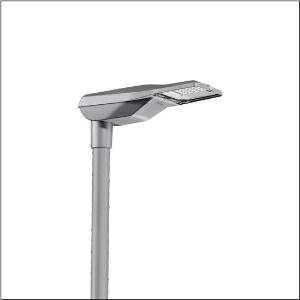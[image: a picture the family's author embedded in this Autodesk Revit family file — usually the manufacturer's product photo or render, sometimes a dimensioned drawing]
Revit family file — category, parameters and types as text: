
# Revit family: streetlight_sl_21_iq_micro___st0_8a_5xe1c41d08cb_e31f
name_source: partatom
category: Lighting Fixtures
units: mm (PartAtom-declared; Revit-internal decimal feet)

## family parameters
Cut with Voids When Loaded = No
Host = Face
Light Source = No
Part Type = Normal
Room Calculation Point = No
Round Connector Dimension = Use Diameter
Shared = No

## types (1)
- --- (1 x LED, 2980 lm, 19.4 W, 4000K)
    Apparent Load = 19 VA
    CIE Flux Codes = 38 75 97 100 100
    Color Rendering = 70
    Color Temperature = 4000K
    Default Elevation = 1800 mm
    Description = Streetlight SL 21 iQ micro, mast luminaire, primary light control with lens, of PMMA, primary optical cover: cover, of toughened safety glass, transparent, light distribution: ST0.8a, light emission: direct distribution, primary light characteristic: asymmetric, installation type: post-top, side-entry, LED, High Power LED, rated luminous flux: 2.980lm, luminous efficacy: 154lm/W, light colour: 740, colour temperature: 4000K, control: Auto-Match, Temp-Guard, Lumen-Switch, Night-Set, Smart-Wire, Light-Fading, Desk-Remote (wireless, voltage-free reading and setting of iQ features in the workshop via application-optimized NFC function/RFID function), optimised constant luminous flux control (CLO 2.0), pre-setting: linear dimming characteristic, mains connection: 220..240V, AC, 50/60Hz, start of lifetime: 19W, end of service life: 20W, reduction: 10W, luminaire housing, of diecast aluminium, powder-coated, Siteco® metallic grey (DB 702S), corrosivity category C5 mid according to DIN EN ISO 12944, please order mast flange separately, inclination adjustable: 0°, 5°, 10°, 15°, sealing non-destructively replaceable, multi-level sealing system, length: 528mm, width: 235mm, height: 110mm, mast flange for spigot size: 42mm (side-entry): 5XC10008XM4, 60/48mm (side-entry/post-top): 5XC10108XM2, 76/60mm (side-entry/post-top): 5XC10108XM1, protection rating (complete): IP66, insulation class (complete): insulation class II (safety insulation), certification: CE, ENEC, ENEC+, VDE, impact resistance: IK09, permissible operating ambient temperature for outdoor applications: -40..+50°C, standard-compliant lighting for roads and squares, packaging unit: 1 piece

Light Distribution: ST0.8a
    Height = 110 mm
    Lamp = 1 x LED
    Lamp Light Flux = 2980 lm
    Lamp Power = 19.4 W
    Lamp count = 1
    Length = 528 mm
    Luminous efficacy = 154 lm/W
    Manufacturer = Siteco
    ModVariant = No
    Model = 5XE1C41D08CB
    Number of Poles = 1
    OnlyDefault = Yes
    Power Factor = 1
    Product Name = Streetlight SL 21 iQ micro | ST0.8a
    Product group = mast luminaire | pylon top
    ProductGroupID = 6100
    Protection Class = Protection class II
    Protection Degree = IP 66
    RLX_Detail_Level = 1
    RLX_Emergency_Light_Flux = 0 lm
    RLX_Emergency_Type = 0
    RLX_Emergency_Type_DB = No
    RlxData = <blob elided: 98709 chars, md5=6c8b925f>
    Socket = socket
    Standby Power = 0 W
    System Light Flux = 2980 lm
    System Power = 19 W
    Type Comments = factory setting: luminous flux: 100 % | dim-lin: 254 | 387 mA
    Type Image = l_1006881.jpg
    URL = http://relux.com
    VarID = @adj_108195
    Voltage = 0 V
    Weight = 0.00 kg
    Width = 235 mm

## geometry (parser evidence)
native form markers: Blend x4, Sweep x12
no freeform markers — native parametric forms only
